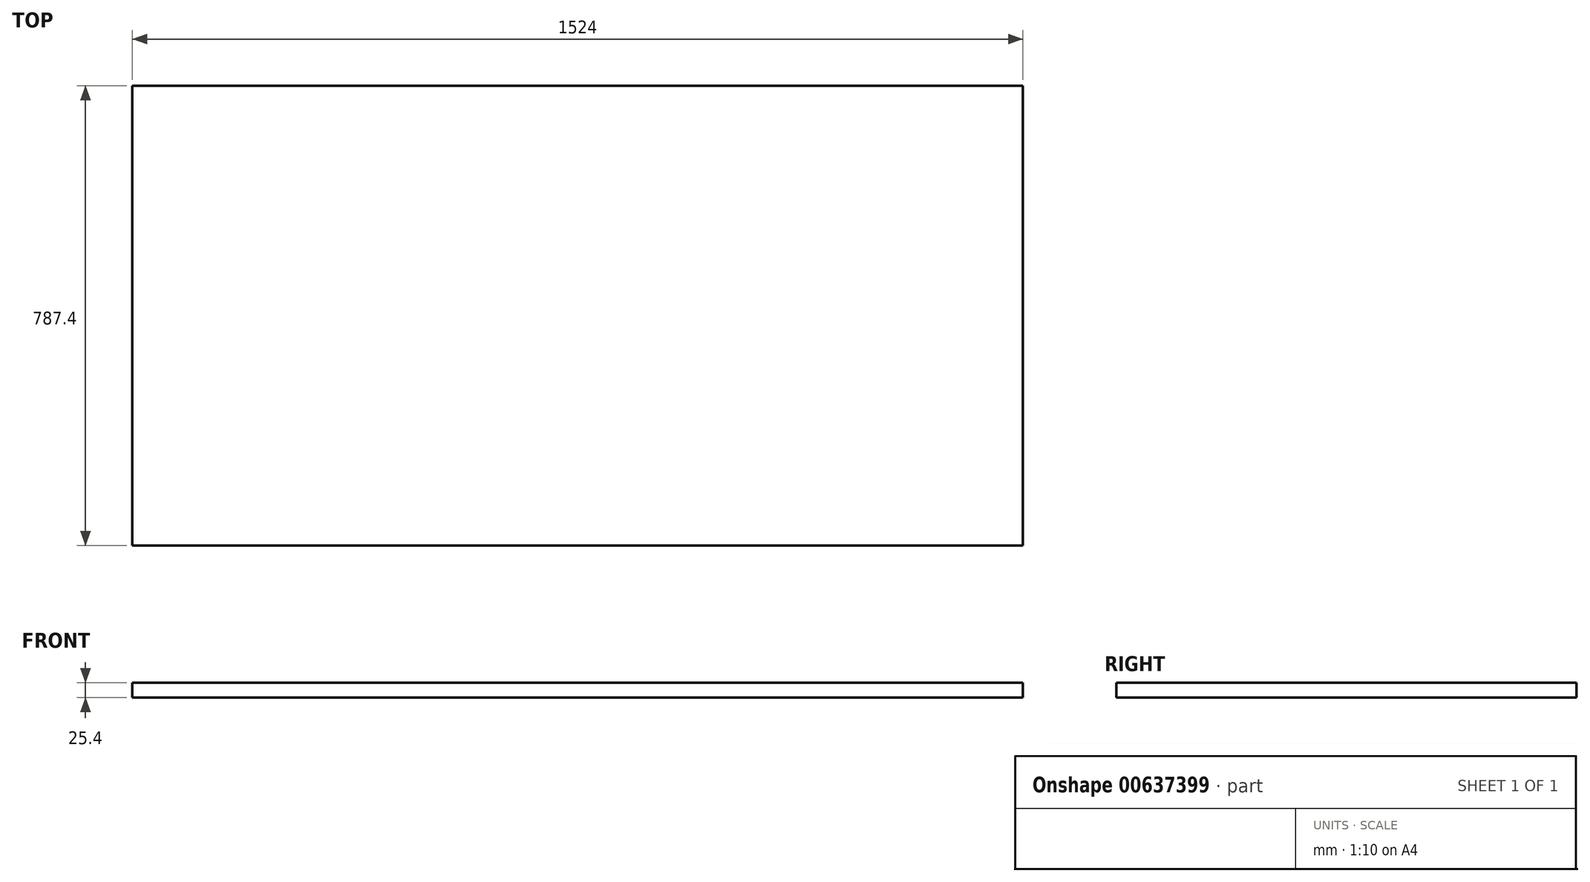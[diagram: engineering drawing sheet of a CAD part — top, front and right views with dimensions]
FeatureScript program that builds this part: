
annotation { "Feature Type Name" : "Feature", "Feature Type Description" : "" }
export const myFeature = defineFeature(function(context is Context, id is Id, definition is map)
    precondition{}
    {
        {
            var Q0;
            Q0=qCreatedBy(makeId("Top.planeOp"),FACE);
            var sketch = newSketch(context, id + "F0", { "sketchPlane" : qUnion([Q0])});
            skLineSegment(sketch, "E0.bottom", {"start": v(-757.53, -334.8) * mm, "end": v(766.47, -334.8) * mm});
            skLineSegment(sketch, "E0.top", {"start": v(-757.53, 452.6) * mm, "end": v(766.47, 452.6) * mm});
            skLineSegment(sketch, "E0.left", {"start": v(-757.53, -334.8) * mm, "end": v(-757.53, 452.6) * mm});
            skLineSegment(sketch, "E0.right", {"start": v(766.47, -334.8) * mm, "end": v(766.47, 452.6) * mm});
            skSolve(sketch);
        }
        {
            var Q0;
            Q0 = qSketchRegion(id + "F0", true);
            extrude(context, id + "F1", {"entities" : qUnion([Q0]), "depth" : 25.4 * mm, "offsetDistance" : 25.4 * mm});
        }
    });
